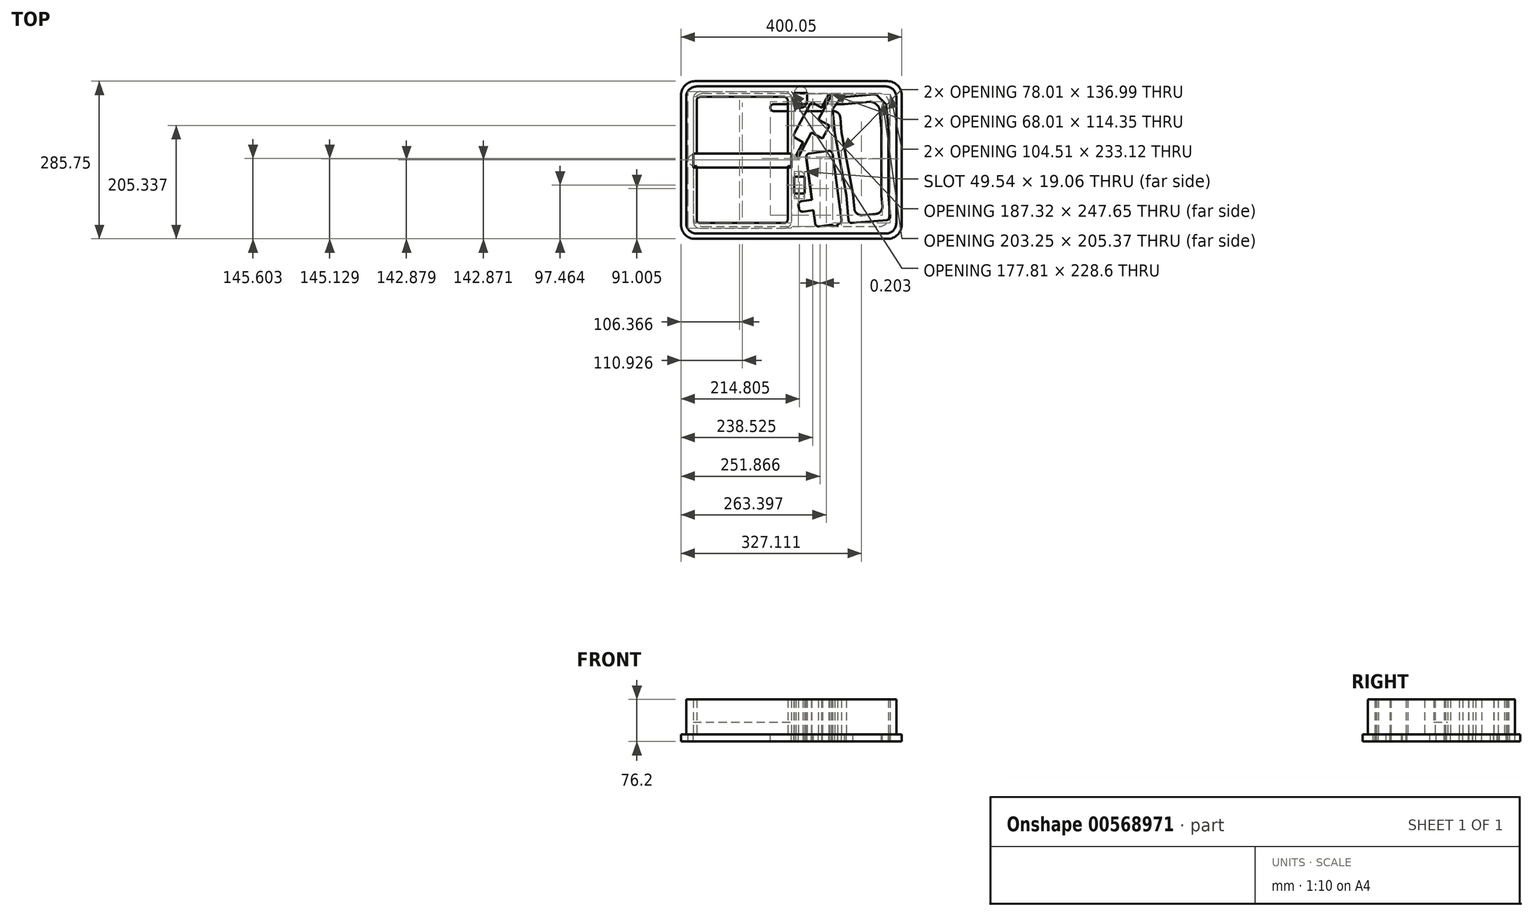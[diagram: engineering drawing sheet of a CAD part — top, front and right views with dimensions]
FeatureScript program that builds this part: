
annotation { "Feature Type Name" : "Feature", "Feature Type Description" : "" }
export const myFeature = defineFeature(function(context is Context, id is Id, definition is map)
    precondition{}
    {
        {
            var Q0;
            Q0=qCreatedBy(makeId("Top.planeOp"),FACE);
            var sketch = newSketch(context, id + "F0", { "sketchPlane" : qUnion([Q0])});
            skLineSegment(sketch, "E0.bottom", {"start": v(-171.53, 124.16) * mm, "end": v(171.37, 124.16) * mm});
            skLineSegment(sketch, "E0.top", {"start": v(-171.53, -142.54) * mm, "end": v(171.37, -142.54) * mm});
            skLineSegment(sketch, "E0.left", {"start": v(-190.58, 105.11) * mm, "end": v(-190.58, -123.49) * mm});
            skLineSegment(sketch, "E0.right", {"start": v(190.42, 105.11) * mm, "end": v(190.42, -123.49) * mm});
            skLineSegment(sketch, "E1.bottom", {"start": v(-165.18, 105.11) * mm, "end": v(-12.78, 105.11) * mm});
            skLineSegment(sketch, "E1.top", {"start": v(-165.18, -123.49) * mm, "end": v(-12.78, -123.49) * mm});
            skLineSegment(sketch, "E1.left", {"start": v(-171.53, 98.76) * mm, "end": v(-171.53, 2.24) * mm});
            skLineSegment(sketch, "E1.right", {"start": v(-6.43, 98.76) * mm, "end": v(-6.43, 2.24) * mm});
            skLineSegment(sketch, "E2.bottom", {"start": v(5.16, -39.36) * mm, "end": v(24.21, -39.36) * mm});
            skLineSegment(sketch, "E2.top", {"start": v(5.16, -69.84) * mm, "end": v(24.21, -69.84) * mm});
            skLineSegment(sketch, "E2.left", {"start": v(5.16, -39.36) * mm, "end": v(5.16, -69.84) * mm});
            skLineSegment(sketch, "E2.right", {"start": v(24.21, -39.36) * mm, "end": v(24.21, -69.84) * mm});
            skLineSegment(sketch, "E3", {"start": v(-25.48, 88.56) * mm, "end": v(62.79, 41.28) * mm, "construction": true});
            skLineSegment(sketch, "E4", {"start": v(19.13, 64.67) * mm, "end": v(5.33, 38.92) * mm});
            skLineSegment(sketch, "E5", {"start": v(7.93, 30.33) * mm, "end": v(21.37, 23.13) * mm});
            skLineSegment(sketch, "E6", {"start": v(21.37, 23.13) * mm, "end": v(8.17, -1.5) * mm});
            skLineSegment(sketch, "E7", {"start": v(8.17, -1.5) * mm, "end": v(12.65, -3.9) * mm});
            skLineSegment(sketch, "E8", {"start": v(48.93, 63.83) * mm, "end": v(69.08, 53.04) * mm});
            skLineSegment(sketch, "E9", {"start": v(69.08, 53.04) * mm, "end": v(62.79, 41.28) * mm});
            skPoint(sketch, "E10.visualSharp", {"position": v(2.33, 33.32) * mm});
            skArc(sketch, "E10.filletArc", {"start": v(5.33, 38.92) * mm, "mid": v(4.85, 34.09) * mm, "end": v(7.93, 30.33) * mm});
            skArc(sketch, "E11.MirrorCS", {"start": v(32.92, 90.42) * mm, "mid": v(36.68, 93.5) * mm, "end": v(41.51, 93.02) * mm});
            skLineSegment(sketch, "E12.MirrorCS", {"start": v(54.95, 85.82) * mm, "end": v(68.14, 110.45) * mm});
            skLineSegment(sketch, "E13.MirrorCS", {"start": v(41.51, 93.02) * mm, "end": v(54.95, 85.82) * mm});
            skPoint(sketch, "E14.MirrorP", {"position": v(35.92, 96.02) * mm});
            skLineSegment(sketch, "E15.MirrorCS", {"start": v(36.34, 40.32) * mm, "end": v(56.49, 29.53) * mm});
            skLineSegment(sketch, "E16.MirrorCS", {"start": v(19.13, 64.67) * mm, "end": v(32.92, 90.42) * mm});
            skLineSegment(sketch, "E17.MirrorCS", {"start": v(56.49, 29.53) * mm, "end": v(62.79, 41.28) * mm});
            skLineSegment(sketch, "E18", {"start": v(36.34, 40.32) * mm, "end": v(12.65, -3.9) * mm});
            skPoint(sketch, "E19.visualSharp", {"position": v(-190.58, 124.16) * mm});
            skArc(sketch, "E19.filletArc", {"start": v(-171.53, 124.16) * mm, "mid": v(-185, 118.58) * mm, "end": v(-190.58, 105.11) * mm});
            skPoint(sketch, "E20.visualSharp", {"position": v(190.42, 124.16) * mm});
            skArc(sketch, "E20.filletArc", {"start": v(190.42, 105.11) * mm, "mid": v(184.84, 118.58) * mm, "end": v(171.37, 124.16) * mm});
            skPoint(sketch, "E21.visualSharp", {"position": v(190.42, -142.54) * mm});
            skArc(sketch, "E21.filletArc", {"start": v(171.37, -142.54) * mm, "mid": v(184.84, -136.96) * mm, "end": v(190.42, -123.49) * mm});
            skPoint(sketch, "E22.visualSharp", {"position": v(-190.58, -142.54) * mm});
            skArc(sketch, "E22.filletArc", {"start": v(-190.58, -123.49) * mm, "mid": v(-185, -136.96) * mm, "end": v(-171.53, -142.54) * mm});
            skArc(sketch, "E23.filletArc", {"start": v(-165.18, 105.11) * mm, "mid": v(-169.67, 103.25) * mm, "end": v(-171.53, 98.76) * mm});
            skArc(sketch, "E24.filletArc", {"start": v(-171.53, -117.14) * mm, "mid": v(-169.67, -121.63) * mm, "end": v(-165.18, -123.49) * mm});
            skPoint(sketch, "E25.visualSharp", {"position": v(-6.43, 105.11) * mm});
            skArc(sketch, "E25.filletArc", {"start": v(-6.43, 98.76) * mm, "mid": v(-8.3, 103.25) * mm, "end": v(-12.78, 105.11) * mm});
            skPoint(sketch, "E26.visualSharp", {"position": v(-6.43, -123.49) * mm});
            skArc(sketch, "E26.filletArc", {"start": v(-12.78, -123.49) * mm, "mid": v(-8.3, -121.63) * mm, "end": v(-6.43, -117.14) * mm});
            skLineSegment(sketch, "E27.bottom", {"start": v(32.42, 2.65) * mm, "end": v(67.66, 7.4) * mm});
            skLineSegment(sketch, "E27.top", {"start": v(50.23, -129.5) * mm, "end": v(73.2, -126.41) * mm});
            skLineSegment(sketch, "E27.left", {"start": v(26.98, -4.5) * mm, "end": v(37.15, -80) * mm});
            skLineSegment(sketch, "E27.right", {"start": v(74.8, 1.95) * mm, "end": v(90.91, -117.62) * mm});
            skLineSegment(sketch, "E28.bottom", {"start": v(36.06, -81.44) * mm, "end": v(18.44, -83.81) * mm});
            skLineSegment(sketch, "E28.top", {"start": v(38.6, -100.32) * mm, "end": v(20.99, -102.7) * mm});
            skLineSegment(sketch, "E28.right", {"start": v(13, -90.95) * mm, "end": v(13.84, -97.25) * mm});
            skLineSegment(sketch, "E29.trimOffspring", {"start": v(40.03, -101.4) * mm, "end": v(43.09, -124.06) * mm});
            skLineSegment(sketch, "E30", {"start": v(37.32, -81.27) * mm, "end": v(39.86, -100.15) * mm, "construction": true});
            skPoint(sketch, "E31.visualSharp", {"position": v(26.13, 1.8) * mm});
            skArc(sketch, "E31.filletArc", {"start": v(32.42, 2.65) * mm, "mid": v(28.22, 0.2) * mm, "end": v(26.98, -4.5) * mm});
            skPoint(sketch, "E32.visualSharp", {"position": v(43.93, -130.35) * mm});
            skArc(sketch, "E32.filletArc", {"start": v(43.09, -124.06) * mm, "mid": v(45.53, -128.26) * mm, "end": v(50.23, -129.5) * mm});
            skPoint(sketch, "E33.visualSharp", {"position": v(91.76, -123.91) * mm});
            skArc(sketch, "E33.filletArc", {"start": v(85.47, -124.76) * mm, "mid": v(89.67, -122.32) * mm, "end": v(90.91, -117.62) * mm});
            skPoint(sketch, "E34.visualSharp", {"position": v(73.96, 8.24) * mm});
            skArc(sketch, "E34.filletArc", {"start": v(74.8, 1.95) * mm, "mid": v(72.36, 6.15) * mm, "end": v(67.66, 7.4) * mm});
            skPoint(sketch, "E35.visualSharp", {"position": v(12.15, -84.66) * mm});
            skArc(sketch, "E35.filletArc", {"start": v(18.44, -83.81) * mm, "mid": v(14.24, -86.25) * mm, "end": v(13, -90.95) * mm});
            skPoint(sketch, "E36.visualSharp", {"position": v(14.7, -103.54) * mm});
            skArc(sketch, "E36.filletArc", {"start": v(13.84, -97.25) * mm, "mid": v(16.29, -101.45) * mm, "end": v(20.99, -102.7) * mm});
            skLineSegment(sketch, "E37.bottom", {"start": v(5.33, 112.5) * mm, "end": v(28.44, 112.5) * mm});
            skLineSegment(sketch, "E37.left", {"start": v(5.33, 112.5) * mm, "end": v(5.33, 97.27) * mm});
            skLineSegment(sketch, "E37.right", {"start": v(28.44, 112.5) * mm, "end": v(28.44, 97.27) * mm});
            skArc(sketch, "E38", {"start": v(5.33, 97.27) * mm, "mid": v(16.89, 85.7) * mm, "end": v(28.44, 97.27) * mm});
            skLineSegment(sketch, "E39.bottom", {"start": v(73, 102.67) * mm, "end": v(170.4, 111.39) * mm, "construction": true});
            skLineSegment(sketch, "E39.top", {"start": v(93.38, -125.02) * mm, "end": v(190.78, -116.3) * mm, "construction": true});
            skLineSegment(sketch, "E39.left", {"start": v(73, 102.67) * mm, "end": v(93.38, -125.02) * mm, "construction": true});
            skLineSegment(sketch, "E39.right", {"start": v(170.4, 111.39) * mm, "end": v(190.78, -116.3) * mm, "construction": true});
            skLineSegment(sketch, "E40", {"start": v(121.7, 107.03) * mm, "end": v(142.08, -120.66) * mm, "construction": true});
            skLineSegment(sketch, "E41", {"start": v(90.08, 104.2) * mm, "end": v(110.45, -123.49) * mm, "construction": true});
            skLineSegment(sketch, "E42.MirrorCS", {"start": v(153.33, 109.86) * mm, "end": v(173.7, -117.83) * mm, "construction": true});
            skLineSegment(sketch, "E43", {"start": v(83.76, 103.64) * mm, "end": v(104.13, -124.06) * mm, "construction": true});
            skLineSegment(sketch, "E44.MirrorCS", {"start": v(159.65, 110.43) * mm, "end": v(180.02, -117.26) * mm, "construction": true});
            skLineSegment(sketch, "E45", {"start": v(74.76, 83.07) * mm, "end": v(172.16, 91.78) * mm, "construction": true});
            skLineSegment(sketch, "E46", {"start": v(78.66, 39.43) * mm, "end": v(176.06, 48.14) * mm, "construction": true});
            skLineSegment(sketch, "E47", {"start": v(89.41, -80.74) * mm, "end": v(186.82, -72.03) * mm, "construction": true});
            skLineSegment(sketch, "E48", {"start": v(92.96, 104.46) * mm, "end": v(150.45, 109.6) * mm});
            skLineSegment(sketch, "E49", {"start": v(155.41, 107.86) * mm, "end": v(170.44, 93.43) * mm});
            skLineSegment(sketch, "E50", {"start": v(172.37, 89.41) * mm, "end": v(176.06, 48.14) * mm});
            skLineSegment(sketch, "E51", {"start": v(176.06, 48.14) * mm, "end": v(176.06, -73) * mm});
            skLineSegment(sketch, "E52", {"start": v(176.06, -73) * mm, "end": v(179.46, -110.94) * mm});
            skLineSegment(sketch, "E53", {"start": v(173.7, -117.83) * mm, "end": v(110.45, -123.49) * mm});
            skLineSegment(sketch, "E54", {"start": v(103.56, -117.73) * mm, "end": v(99.56, -73) * mm});
            skLineSegment(sketch, "E55", {"start": v(99.56, -73) * mm, "end": v(78.66, 39.43) * mm});
            skLineSegment(sketch, "E56", {"start": v(78.66, 39.43) * mm, "end": v(74.97, 80.7) * mm});
            skLineSegment(sketch, "E57", {"start": v(76.15, 85) * mm, "end": v(88.38, 101.86) * mm});
            skPoint(sketch, "E58.visualSharp", {"position": v(104.13, -124.06) * mm});
            skArc(sketch, "E58.filletArc", {"start": v(103.56, -117.73) * mm, "mid": v(105.81, -122.04) * mm, "end": v(110.45, -123.49) * mm});
            skPoint(sketch, "E59.visualSharp", {"position": v(180.02, -117.26) * mm});
            skArc(sketch, "E59.filletArc", {"start": v(173.7, -117.83) * mm, "mid": v(178, -115.58) * mm, "end": v(179.46, -110.94) * mm});
            skPoint(sketch, "E60.visualSharp", {"position": v(90.08, 104.2) * mm});
            skArc(sketch, "E60.filletArc", {"start": v(92.96, 104.46) * mm, "mid": v(90.39, 103.66) * mm, "end": v(88.38, 101.86) * mm});
            skPoint(sketch, "E61.visualSharp", {"position": v(74.76, 83.07) * mm});
            skArc(sketch, "E61.filletArc", {"start": v(76.15, 85) * mm, "mid": v(75.17, 82.95) * mm, "end": v(74.97, 80.7) * mm});
            skPoint(sketch, "E62.visualSharp", {"position": v(153.33, 109.86) * mm});
            skArc(sketch, "E62.filletArc", {"start": v(155.41, 107.86) * mm, "mid": v(153.12, 109.27) * mm, "end": v(150.45, 109.6) * mm});
            skPoint(sketch, "E63.visualSharp", {"position": v(172.16, 91.78) * mm});
            skArc(sketch, "E63.filletArc", {"start": v(172.37, 89.41) * mm, "mid": v(171.77, 91.6) * mm, "end": v(170.44, 93.43) * mm});
            skLineSegment(sketch, "E64", {"start": v(5.33, 97.27) * mm, "end": v(28.44, 97.27) * mm, "construction": true});
            skLineSegment(sketch, "E65.MirrorCS", {"start": v(48.93, 63.83) * mm, "end": v(72.62, 108.05) * mm});
            skLineSegment(sketch, "E66.MirrorCS", {"start": v(68.14, 110.45) * mm, "end": v(72.62, 108.05) * mm});
            skLineSegment(sketch, "E67", {"start": v(84.07, -126.23) * mm, "end": v(84.15, -126.86) * mm});
            skLineSegment(sketch, "E68", {"start": v(83.06, -128.29) * mm, "end": v(76.14, -129.22) * mm});
            skLineSegment(sketch, "E69", {"start": v(74.71, -128.13) * mm, "end": v(74.63, -127.5) * mm});
            skLineSegment(sketch, "E70", {"start": v(85.15, -124.8) * mm, "end": v(85.47, -124.76) * mm});
            skPoint(sketch, "E71.visualSharp", {"position": v(39.86, -100.15) * mm});
            skArc(sketch, "E71.filletArc", {"start": v(40.03, -101.4) * mm, "mid": v(39.55, -100.57) * mm, "end": v(38.6, -100.32) * mm});
            skPoint(sketch, "E72.visualSharp", {"position": v(37.32, -81.27) * mm});
            skArc(sketch, "E72.filletArc", {"start": v(36.06, -81.44) * mm, "mid": v(36.9, -80.95) * mm, "end": v(37.15, -80) * mm});
            skPoint(sketch, "E73.visualSharp", {"position": v(74.88, -129.39) * mm});
            skArc(sketch, "E73.filletArc", {"start": v(74.71, -128.13) * mm, "mid": v(75.2, -128.97) * mm, "end": v(76.14, -129.22) * mm});
            skPoint(sketch, "E74.visualSharp", {"position": v(84.32, -128.12) * mm});
            skArc(sketch, "E74.filletArc", {"start": v(83.06, -128.29) * mm, "mid": v(83.9, -127.8) * mm, "end": v(84.15, -126.86) * mm});
            skPoint(sketch, "E75.visualSharp", {"position": v(83.9, -124.97) * mm});
            skArc(sketch, "E75.filletArc", {"start": v(85.15, -124.8) * mm, "mid": v(84.31, -125.29) * mm, "end": v(84.07, -126.23) * mm});
            skPoint(sketch, "E76.visualSharp", {"position": v(74.46, -126.24) * mm});
            skArc(sketch, "E76.filletArc", {"start": v(74.63, -127.5) * mm, "mid": v(74.14, -126.66) * mm, "end": v(73.2, -126.41) * mm});
            skLineSegment(sketch, "E77", {"start": v(73.2, -126.41) * mm, "end": v(85.15, -124.8) * mm, "construction": true});
            skLineSegment(sketch, "E78", {"start": v(-171.53, 2.24) * mm, "end": v(-177.9, 2.24) * mm});
            skLineSegment(sketch, "E79", {"start": v(-88.98, 105.11) * mm, "end": v(-88.98, -123.49) * mm, "construction": true});
            skLineSegment(sketch, "E80", {"start": v(-177.9, 2.24) * mm, "end": v(-177.9, -20.62) * mm});
            skLineSegment(sketch, "E81", {"start": v(-177.9, -20.62) * mm, "end": v(-171.53, -20.62) * mm});
            skLineSegment(sketch, "E82.MirrorCS", {"start": v(-6.43, 2.24) * mm, "end": v(-0.08, 2.24) * mm});
            skLineSegment(sketch, "E83.MirrorCS", {"start": v(-0.08, 2.24) * mm, "end": v(-0.08, -20.62) * mm});
            skLineSegment(sketch, "E84.MirrorCS", {"start": v(-0.08, -20.62) * mm, "end": v(-6.43, -20.62) * mm});
            skLineSegment(sketch, "E85", {"start": v(-171.53, -9.19) * mm, "end": v(-6.43, -9.19) * mm, "construction": true});
            skLineSegment(sketch, "E86", {"start": v(-177.9, -9.19) * mm, "end": v(-171.53, -9.19) * mm, "construction": true});
            skLineSegment(sketch, "E87", {"start": v(-171.53, 2.24) * mm, "end": v(-171.53, -20.62) * mm, "construction": true});
            skLineSegment(sketch, "E88", {"start": v(-171.53, -20.62) * mm, "end": v(-171.53, -117.14) * mm});
            skLineSegment(sketch, "E89", {"start": v(-6.43, 2.24) * mm, "end": v(-6.43, -20.62) * mm, "construction": true});
            skLineSegment(sketch, "E90", {"start": v(-6.43, -20.62) * mm, "end": v(-6.43, -117.14) * mm});
            skSolve(sketch);
        }
        {
            var Q0;
            Q0 = qSketchRegion(id + "F0", true);
            extrude(context, id + "F1", {"entities" : qUnion([Q0]), "depth" : 63.5 * mm, "offsetDistance" : 25.4 * mm});
        }
        {
            var Q0;
            Q0=qCreatedBy(makeId("Top.planeOp"),FACE);
            var sketch = newSketch(context, id + "F2", { "sketchPlane" : qUnion([Q0])});
            skLineSegment(sketch, "E91.0", {"start": v(-190.58, 124.16) * mm, "end": v(190.42, 124.16) * mm, "construction": true});
            skLineSegment(sketch, "E92.0", {"start": v(-190.58, 124.16) * mm, "end": v(-190.58, -142.54) * mm, "construction": true});
            skLineSegment(sketch, "E93.0", {"start": v(190.42, 124.16) * mm, "end": v(190.42, -142.54) * mm, "construction": true});
            skLineSegment(sketch, "E94.0", {"start": v(-190.26, -142.54) * mm, "end": v(190.42, -142.54) * mm, "construction": true});
            skPoint(sketch, "E95.orphan", {"position": v(-171.53, 124.16) * mm});
            skPoint(sketch, "E96.orphan", {"position": v(-190.58, 105.11) * mm});
            skPoint(sketch, "E97.orphan", {"position": v(171.37, 124.16) * mm});
            skPoint(sketch, "E98.orphan", {"position": v(190.42, 105.11) * mm});
            skPoint(sketch, "E99.orphan", {"position": v(190.42, -123.49) * mm});
            skPoint(sketch, "E100.orphan", {"position": v(171.37, -142.54) * mm});
            skPoint(sketch, "E101.orphan", {"position": v(-171.53, -142.54) * mm});
            skPoint(sketch, "E102.orphan", {"position": v(-190.58, -123.49) * mm});
            skPoint(sketch, "E103", {"position": v(0, 0) * mm});
            skLineSegment(sketch, "E104", {"start": v(-0.08, 124.16) * mm, "end": v(-0.08, -142.54) * mm, "construction": true});
            skPoint(sketch, "E104.startSnap0", {"position": v(-0.08, 124.16) * mm});
            skLineSegment(sketch, "E105", {"start": v(-190.58, -9.19) * mm, "end": v(190.42, -9.19) * mm, "construction": true});
            skPoint(sketch, "E106", {"position": v(-0.08, -9.19) * mm});
            skLineSegment(sketch, "E107.bottom", {"start": v(-158.83, 111.46) * mm, "end": v(158.67, 111.46) * mm});
            skLineSegment(sketch, "E107.top", {"start": v(-158.83, -129.84) * mm, "end": v(158.67, -129.84) * mm});
            skLineSegment(sketch, "E107.left", {"start": v(-177.88, 92.41) * mm, "end": v(-177.88, 9.86) * mm});
            skLineSegment(sketch, "E107.right", {"start": v(177.72, 92.41) * mm, "end": v(177.72, -110.79) * mm});
            skPoint(sketch, "E108.visualSharp", {"position": v(-177.88, 111.46) * mm});
            skPoint(sketch, "E109.visualSharp", {"position": v(177.72, 111.46) * mm});
            skPoint(sketch, "E110.visualSharp", {"position": v(177.72, -129.84) * mm});
            skPoint(sketch, "E111.visualSharp", {"position": v(-177.88, -129.84) * mm});
            skLineSegment(sketch, "E112.0.0", {"start": v(99.56, -73) * mm, "end": v(103.56, -117.73) * mm, "construction": true});
            skArc(sketch, "E112.0.1", {"start": v(103.56, -117.73) * mm, "mid": v(105.81, -122.04) * mm, "end": v(110.45, -123.49) * mm, "construction": true});
            skLineSegment(sketch, "E112.0.2", {"start": v(110.45, -123.49) * mm, "end": v(173.7, -117.83) * mm, "construction": true});
            skArc(sketch, "E112.0.3", {"start": v(173.7, -117.83) * mm, "mid": v(178, -115.58) * mm, "end": v(179.46, -110.94) * mm, "construction": true});
            skLineSegment(sketch, "E112.0.4", {"start": v(179.46, -110.94) * mm, "end": v(176.06, -73) * mm, "construction": true});
            skLineSegment(sketch, "E112.0.5", {"start": v(176.06, -73) * mm, "end": v(176.06, 48.14) * mm, "construction": true});
            skLineSegment(sketch, "E112.0.6", {"start": v(176.06, 48.14) * mm, "end": v(172.37, 89.41) * mm, "construction": true});
            skArc(sketch, "E112.0.7", {"start": v(172.37, 89.41) * mm, "mid": v(171.77, 91.6) * mm, "end": v(170.44, 93.43) * mm, "construction": true});
            skLineSegment(sketch, "E112.0.8", {"start": v(170.44, 93.43) * mm, "end": v(155.41, 107.86) * mm, "construction": true});
            skArc(sketch, "E112.0.9", {"start": v(155.41, 107.86) * mm, "mid": v(153.12, 109.27) * mm, "end": v(150.45, 109.6) * mm, "construction": true});
            skLineSegment(sketch, "E112.0.10", {"start": v(150.45, 109.6) * mm, "end": v(92.96, 104.46) * mm, "construction": true});
            skArc(sketch, "E112.0.11", {"start": v(92.96, 104.46) * mm, "mid": v(90.39, 103.66) * mm, "end": v(88.38, 101.86) * mm, "construction": true});
            skLineSegment(sketch, "E112.0.12", {"start": v(88.38, 101.86) * mm, "end": v(76.15, 85) * mm, "construction": true});
            skArc(sketch, "E112.0.13", {"start": v(76.15, 85) * mm, "mid": v(75.17, 82.95) * mm, "end": v(74.97, 80.7) * mm, "construction": true});
            skLineSegment(sketch, "E112.0.14", {"start": v(74.97, 80.7) * mm, "end": v(78.66, 39.43) * mm, "construction": true});
            skLineSegment(sketch, "E112.0.15", {"start": v(78.66, 39.43) * mm, "end": v(99.56, -73) * mm, "construction": true});
            skLineSegment(sketch, "E113.0", {"start": v(88.87, 67.9) * mm, "end": v(91.26, 41.16) * mm});
            skLineSegment(sketch, "E113.1", {"start": v(96.97, 92.07) * mm, "end": v(87.83, 79.46) * mm, "construction": true});
            skLineSegment(sketch, "E113.2", {"start": v(91.26, 41.16) * mm, "end": v(112.15, -71.26) * mm});
            skLineSegment(sketch, "E113.3", {"start": v(142.94, 96.18) * mm, "end": v(96.97, 92.07) * mm});
            skLineSegment(sketch, "E113.4", {"start": v(156.5, 89.2) * mm, "end": v(152.87, 92.7) * mm});
            skLineSegment(sketch, "E113.5", {"start": v(163.36, 47.57) * mm, "end": v(160.36, 81.18) * mm});
            skLineSegment(sketch, "E113.6", {"start": v(112.15, -71.26) * mm, "end": v(114.51, -97.62) * mm});
            skLineSegment(sketch, "E113.7", {"start": v(128.3, -109.14) * mm, "end": v(153.6, -106.88) * mm});
            skLineSegment(sketch, "E113.8", {"start": v(165.11, -93.1) * mm, "end": v(163.36, -73.56) * mm});
            skLineSegment(sketch, "E113.9", {"start": v(163.36, -73.56) * mm, "end": v(163.36, 47.57) * mm});
            skLineSegment(sketch, "E114", {"start": v(96.97, 92.07) * mm, "end": v(-31.83, 92.07) * mm});
            skLineSegment(sketch, "E115", {"start": v(-31.83, 92.07) * mm, "end": v(-31.83, 79.46) * mm, "construction": true});
            skLineSegment(sketch, "E116", {"start": v(-31.83, 79.46) * mm, "end": v(76.22, 79.46) * mm});
            skArc(sketch, "E117", {"start": v(-31.83, 92.07) * mm, "mid": v(-38.14, 85.76) * mm, "end": v(-31.83, 79.46) * mm});
            skPoint(sketch, "E118.visualSharp", {"position": v(115.65, -110.27) * mm});
            skArc(sketch, "E118.filletArc", {"start": v(114.51, -97.62) * mm, "mid": v(119.02, -106.24) * mm, "end": v(128.3, -109.14) * mm});
            skPoint(sketch, "E119.visualSharp", {"position": v(166.24, -105.75) * mm});
            skArc(sketch, "E119.filletArc", {"start": v(153.6, -106.88) * mm, "mid": v(162.2, -102.37) * mm, "end": v(165.11, -93.1) * mm});
            skPoint(sketch, "E120.visualSharp", {"position": v(87.83, 79.46) * mm});
            skArc(sketch, "E120.filletArc", {"start": v(88.87, 67.9) * mm, "mid": v(84.79, 76.13) * mm, "end": v(76.22, 79.46) * mm});
            skPoint(sketch, "E121.visualSharp", {"position": v(148.7, 96.7) * mm});
            skArc(sketch, "E121.filletArc", {"start": v(152.87, 92.7) * mm, "mid": v(148.29, 95.51) * mm, "end": v(142.94, 96.18) * mm});
            skPoint(sketch, "E122.visualSharp", {"position": v(159.93, 85.91) * mm});
            skArc(sketch, "E122.filletArc", {"start": v(160.36, 81.18) * mm, "mid": v(159.16, 85.54) * mm, "end": v(156.5, 89.2) * mm});
            skArc(sketch, "E123.filletArc", {"start": v(-158.83, 111.46) * mm, "mid": v(-172.3, 105.88) * mm, "end": v(-177.88, 92.41) * mm});
            skArc(sketch, "E124.filletArc", {"start": v(177.72, 92.41) * mm, "mid": v(172.14, 105.88) * mm, "end": v(158.67, 111.46) * mm});
            skArc(sketch, "E125.filletArc", {"start": v(158.67, -129.84) * mm, "mid": v(172.14, -124.26) * mm, "end": v(177.72, -110.79) * mm});
            skArc(sketch, "E126.filletArc", {"start": v(-177.88, -110.79) * mm, "mid": v(-172.3, -124.26) * mm, "end": v(-158.83, -129.84) * mm});
            skLineSegment(sketch, "E127", {"start": v(-177.88, 6.69) * mm, "end": v(-177.88, -25.06) * mm, "construction": true});
            skLineSegment(sketch, "E128", {"start": v(-177.88, -28.24) * mm, "end": v(-177.88, -110.79) * mm});
            skLineSegment(sketch, "E129", {"start": v(-177.88, -28.24) * mm, "end": v(-177.88, 9.86) * mm});
            skSolve(sketch);
        }
        {
            var Q0;
            Q0 = qSketchRegion(id + "F2", true);
            extrude(context, id + "F3", {"entities" : qUnion([Q0]), "oppositeDirection" : true, "depth" : 12.7 * mm, "offsetDistance" : 25.4 * mm});
        }
        {
            var Q0;
            Q0=qCreatedBy(makeId("Top.planeOp"),FACE);
            var sketch = newSketch(context, id + "F4", { "sketchPlane" : qUnion([Q0])});
            skLineSegment(sketch, "E130.bottom", {"start": v(-174.5, 133.7) * mm, "end": v(174.74, 133.7) * mm});
            skLineSegment(sketch, "E130.top", {"start": v(-174.5, -152.06) * mm, "end": v(174.74, -152.06) * mm});
            skLineSegment(sketch, "E130.left", {"start": v(-199.9, 108.3) * mm, "end": v(-199.9, -126.66) * mm});
            skLineSegment(sketch, "E130.right", {"start": v(200.14, 108.3) * mm, "end": v(200.14, -126.66) * mm});
            skLineSegment(sketch, "E131.bottom", {"start": v(-164.98, 114.64) * mm, "end": v(-12.58, 114.64) * mm});
            skLineSegment(sketch, "E131.top", {"start": v(-164.98, -133) * mm, "end": v(-12.58, -133) * mm});
            skLineSegment(sketch, "E131.left", {"start": v(-177.68, 101.94) * mm, "end": v(-177.68, 0.34) * mm});
            skLineSegment(sketch, "E131.right", {"start": v(0.12, 101.94) * mm, "end": v(0.12, -120.3) * mm});
            skLineSegment(sketch, "E132.left", {"start": v(5.36, -39.36) * mm, "end": v(5.36, -69.84) * mm});
            skLineSegment(sketch, "E133", {"start": v(-177, 169.84) * mm, "end": v(62.99, 41.3) * mm, "construction": true});
            skLineSegment(sketch, "E134", {"start": v(19.33, 64.68) * mm, "end": v(5.54, 38.93) * mm});
            skLineSegment(sketch, "E135", {"start": v(8.14, 30.33) * mm, "end": v(21.57, 23.14) * mm});
            skLineSegment(sketch, "E136", {"start": v(21.57, 23.14) * mm, "end": v(8.38, -1.5) * mm});
            skLineSegment(sketch, "E137", {"start": v(8.38, -1.5) * mm, "end": v(12.85, -3.89) * mm});
            skLineSegment(sketch, "E138", {"start": v(49.13, 63.84) * mm, "end": v(69.29, 53.05) * mm});
            skLineSegment(sketch, "E139", {"start": v(69.29, 53.05) * mm, "end": v(62.99, 41.3) * mm});
            skPoint(sketch, "E140.visualSharp", {"position": v(2.54, 33.33) * mm});
            skArc(sketch, "E140.filletArc", {"start": v(5.54, 38.93) * mm, "mid": v(5.06, 34.1) * mm, "end": v(8.14, 30.33) * mm});
            skArc(sketch, "E141.MirrorCS", {"start": v(33.12, 90.43) * mm, "mid": v(36.88, 93.5) * mm, "end": v(41.72, 93.03) * mm});
            skLineSegment(sketch, "E142.MirrorCS", {"start": v(55.15, 85.83) * mm, "end": v(68.34, 110.46) * mm});
            skLineSegment(sketch, "E143.MirrorCS", {"start": v(41.72, 93.03) * mm, "end": v(55.15, 85.83) * mm});
            skPoint(sketch, "E144.MirrorP", {"position": v(36.12, 96.03) * mm});
            skLineSegment(sketch, "E145.MirrorCS", {"start": v(36.54, 40.33) * mm, "end": v(56.7, 29.54) * mm});
            skLineSegment(sketch, "E146.MirrorCS", {"start": v(19.33, 64.68) * mm, "end": v(33.12, 90.43) * mm});
            skLineSegment(sketch, "E147.MirrorCS", {"start": v(56.7, 29.54) * mm, "end": v(62.99, 41.3) * mm});
            skLineSegment(sketch, "E148", {"start": v(36.54, 40.33) * mm, "end": v(12.85, -3.89) * mm});
            skPoint(sketch, "E149.visualSharp", {"position": v(-199.9, 133.7) * mm});
            skArc(sketch, "E149.filletArc", {"start": v(-174.5, 133.7) * mm, "mid": v(-192.47, 126.25) * mm, "end": v(-199.9, 108.3) * mm});
            skPoint(sketch, "E150.visualSharp", {"position": v(200.14, 133.7) * mm});
            skArc(sketch, "E150.filletArc", {"start": v(200.14, 108.3) * mm, "mid": v(192.7, 126.25) * mm, "end": v(174.74, 133.7) * mm});
            skPoint(sketch, "E151.visualSharp", {"position": v(200.14, -152.06) * mm});
            skArc(sketch, "E151.filletArc", {"start": v(174.74, -152.06) * mm, "mid": v(192.7, -144.62) * mm, "end": v(200.14, -126.66) * mm});
            skPoint(sketch, "E152.visualSharp", {"position": v(-199.9, -152.06) * mm});
            skArc(sketch, "E152.filletArc", {"start": v(-199.9, -126.66) * mm, "mid": v(-192.47, -144.62) * mm, "end": v(-174.5, -152.06) * mm});
            skPoint(sketch, "E153.visualSharp", {"position": v(-177.68, 114.64) * mm});
            skArc(sketch, "E153.filletArc", {"start": v(-164.98, 114.64) * mm, "mid": v(-173.96, 110.92) * mm, "end": v(-177.68, 101.94) * mm});
            skPoint(sketch, "E154.visualSharp", {"position": v(-177.68, -133) * mm});
            skArc(sketch, "E154.filletArc", {"start": v(-177.68, -120.3) * mm, "mid": v(-173.96, -129.29) * mm, "end": v(-164.98, -133) * mm});
            skPoint(sketch, "E155.visualSharp", {"position": v(0.12, 114.64) * mm});
            skArc(sketch, "E155.filletArc", {"start": v(0.12, 101.94) * mm, "mid": v(-3.6, 110.92) * mm, "end": v(-12.58, 114.64) * mm});
            skPoint(sketch, "E156.visualSharp", {"position": v(0.12, -133) * mm});
            skArc(sketch, "E156.filletArc", {"start": v(-12.58, -133) * mm, "mid": v(-3.6, -129.29) * mm, "end": v(0.12, -120.3) * mm});
            skLineSegment(sketch, "E157.bottom", {"start": v(32.63, 2.66) * mm, "end": v(67.87, 7.4) * mm});
            skLineSegment(sketch, "E157.top", {"start": v(50.43, -129.5) * mm, "end": v(73.39, -126.4) * mm});
            skLineSegment(sketch, "E157.left", {"start": v(27.18, -4.48) * mm, "end": v(37.52, -81.26) * mm});
            skLineSegment(sketch, "E157.right", {"start": v(75, 1.96) * mm, "end": v(91.12, -117.6) * mm});
            skLineSegment(sketch, "E158.top", {"start": v(40.07, -100.14) * mm, "end": v(21.19, -102.68) * mm});
            skLineSegment(sketch, "E158.right", {"start": v(13.2, -90.94) * mm, "end": v(14.05, -97.24) * mm});
            skLineSegment(sketch, "E159.trimOffspring", {"start": v(40.07, -100.14) * mm, "end": v(43.29, -124.05) * mm});
            skLineSegment(sketch, "E160", {"start": v(37.52, -81.26) * mm, "end": v(40.07, -100.14) * mm, "construction": true});
            skPoint(sketch, "E161.visualSharp", {"position": v(26.33, 1.8) * mm});
            skArc(sketch, "E161.filletArc", {"start": v(32.63, 2.66) * mm, "mid": v(28.42, 0.21) * mm, "end": v(27.18, -4.48) * mm});
            skPoint(sketch, "E162.visualSharp", {"position": v(44.14, -130.35) * mm});
            skArc(sketch, "E162.filletArc", {"start": v(43.29, -124.05) * mm, "mid": v(45.73, -128.25) * mm, "end": v(50.43, -129.5) * mm});
            skPoint(sketch, "E163.visualSharp", {"position": v(91.97, -123.9) * mm});
            skArc(sketch, "E163.filletArc", {"start": v(85.67, -124.75) * mm, "mid": v(89.87, -122.3) * mm, "end": v(91.12, -117.6) * mm});
            skPoint(sketch, "E164.visualSharp", {"position": v(74.16, 8.25) * mm});
            skArc(sketch, "E164.filletArc", {"start": v(75, 1.96) * mm, "mid": v(72.57, 6.16) * mm, "end": v(67.87, 7.4) * mm});
            skPoint(sketch, "E165.visualSharp", {"position": v(12.35, -84.65) * mm});
            skPoint(sketch, "E166.visualSharp", {"position": v(14.9, -103.53) * mm});
            skArc(sketch, "E166.filletArc", {"start": v(14.05, -97.24) * mm, "mid": v(16.5, -101.44) * mm, "end": v(21.19, -102.68) * mm});
            skLineSegment(sketch, "E167.bottom", {"start": v(5.53, 112.51) * mm, "end": v(28.65, 112.51) * mm, "construction": true});
            skLineSegment(sketch, "E167.left", {"start": v(5.53, 112.51) * mm, "end": v(5.53, 97.27) * mm});
            skLineSegment(sketch, "E167.right", {"start": v(28.65, 112.51) * mm, "end": v(28.65, 97.27) * mm});
            skArc(sketch, "E168", {"start": v(5.53, 97.27) * mm, "mid": v(17.1, 85.72) * mm, "end": v(28.65, 97.27) * mm});
            skLineSegment(sketch, "E169.bottom", {"start": v(73.2, 102.68) * mm, "end": v(170.6, 111.4) * mm, "construction": true});
            skLineSegment(sketch, "E169.top", {"start": v(93.58, -125) * mm, "end": v(190.98, -116.3) * mm, "construction": true});
            skLineSegment(sketch, "E169.left", {"start": v(73.2, 102.68) * mm, "end": v(93.58, -125) * mm, "construction": true});
            skLineSegment(sketch, "E169.right", {"start": v(170.6, 111.4) * mm, "end": v(190.98, -116.3) * mm, "construction": true});
            skLineSegment(sketch, "E170", {"start": v(121.9, 107.04) * mm, "end": v(142.28, -120.65) * mm, "construction": true});
            skLineSegment(sketch, "E171", {"start": v(90.28, 104.2) * mm, "end": v(110.66, -123.48) * mm, "construction": true});
            skLineSegment(sketch, "E172.MirrorCS", {"start": v(153.53, 109.87) * mm, "end": v(173.9, -117.82) * mm, "construction": true});
            skLineSegment(sketch, "E173", {"start": v(83.96, 103.64) * mm, "end": v(104.33, -124.05) * mm, "construction": true});
            skLineSegment(sketch, "E174.MirrorCS", {"start": v(159.85, 110.43) * mm, "end": v(180.23, -117.26) * mm, "construction": true});
            skLineSegment(sketch, "E175", {"start": v(74.96, 83.07) * mm, "end": v(172.36, 91.79) * mm, "construction": true});
            skLineSegment(sketch, "E176", {"start": v(78.87, 39.43) * mm, "end": v(176.27, 48.15) * mm, "construction": true});
            skLineSegment(sketch, "E177", {"start": v(89.62, -80.74) * mm, "end": v(187.02, -72.02) * mm, "construction": true});
            skLineSegment(sketch, "E178", {"start": v(93.16, 104.47) * mm, "end": v(150.65, 109.61) * mm});
            skLineSegment(sketch, "E179", {"start": v(155.62, 107.87) * mm, "end": v(170.65, 93.44) * mm});
            skLineSegment(sketch, "E180", {"start": v(172.57, 89.42) * mm, "end": v(176.27, 48.15) * mm});
            skLineSegment(sketch, "E181", {"start": v(176.27, 48.15) * mm, "end": v(176.27, -72.98) * mm});
            skLineSegment(sketch, "E182", {"start": v(176.27, -72.98) * mm, "end": v(179.66, -110.93) * mm});
            skLineSegment(sketch, "E183", {"start": v(173.9, -117.82) * mm, "end": v(110.66, -123.48) * mm});
            skLineSegment(sketch, "E184", {"start": v(103.76, -117.72) * mm, "end": v(99.76, -72.98) * mm});
            skLineSegment(sketch, "E185", {"start": v(99.76, -72.98) * mm, "end": v(78.87, 39.43) * mm});
            skLineSegment(sketch, "E186", {"start": v(78.87, 39.43) * mm, "end": v(75.17, 80.7) * mm});
            skLineSegment(sketch, "E187", {"start": v(76.36, 85) * mm, "end": v(88.59, 101.87) * mm});
            skPoint(sketch, "E188.visualSharp", {"position": v(104.33, -124.05) * mm});
            skArc(sketch, "E188.filletArc", {"start": v(103.76, -117.72) * mm, "mid": v(106.02, -122.03) * mm, "end": v(110.66, -123.48) * mm});
            skPoint(sketch, "E189.visualSharp", {"position": v(180.23, -117.26) * mm});
            skArc(sketch, "E189.filletArc", {"start": v(173.9, -117.82) * mm, "mid": v(178.2, -115.57) * mm, "end": v(179.66, -110.93) * mm});
            skPoint(sketch, "E190.visualSharp", {"position": v(90.28, 104.2) * mm});
            skArc(sketch, "E190.filletArc", {"start": v(93.16, 104.47) * mm, "mid": v(90.6, 103.66) * mm, "end": v(88.59, 101.87) * mm});
            skPoint(sketch, "E191.visualSharp", {"position": v(74.96, 83.07) * mm});
            skArc(sketch, "E191.filletArc", {"start": v(76.36, 85) * mm, "mid": v(75.38, 82.96) * mm, "end": v(75.17, 80.7) * mm});
            skPoint(sketch, "E192.visualSharp", {"position": v(153.53, 109.87) * mm});
            skArc(sketch, "E192.filletArc", {"start": v(155.62, 107.87) * mm, "mid": v(153.32, 109.28) * mm, "end": v(150.65, 109.61) * mm});
            skPoint(sketch, "E193.visualSharp", {"position": v(172.36, 91.79) * mm});
            skArc(sketch, "E193.filletArc", {"start": v(172.57, 89.42) * mm, "mid": v(171.97, 91.6) * mm, "end": v(170.65, 93.44) * mm});
            skLineSegment(sketch, "E194", {"start": v(5.53, 97.27) * mm, "end": v(28.65, 97.27) * mm, "construction": true});
            skLineSegment(sketch, "E195.MirrorCS", {"start": v(49.13, 63.84) * mm, "end": v(72.82, 108.06) * mm});
            skLineSegment(sketch, "E196.MirrorCS", {"start": v(68.34, 110.46) * mm, "end": v(72.82, 108.06) * mm});
            skLineSegment(sketch, "E197", {"start": v(0.12, 133.7) * mm, "end": v(0.12, -152.06) * mm, "construction": true});
            skPoint(sketch, "E198.endSnap0", {"position": v(180.8, -2.45) * mm});
            skLineSegment(sketch, "E199", {"start": v(-88.78, 114.64) * mm, "end": v(-88.78, -133) * mm, "construction": true});
            skLineSegment(sketch, "E200", {"start": v(-177.68, -9.18) * mm, "end": v(0.12, -9.18) * mm, "construction": true});
            skLineSegment(sketch, "E201", {"start": v(-199.9, -9.18) * mm, "end": v(200.14, -9.18) * mm, "construction": true});
            skArc(sketch, "E202", {"start": v(5.36, -69.84) * mm, "mid": v(14.9, -79.37) * mm, "end": v(24.43, -69.84) * mm});
            skArc(sketch, "E203", {"start": v(28.65, 112.51) * mm, "mid": v(17.1, 124.07) * mm, "end": v(5.53, 112.51) * mm});
            skArc(sketch, "E204", {"start": v(-177.68, 0.34) * mm, "mid": v(-187.2, -9.18) * mm, "end": v(-177.68, -18.7) * mm});
            skLineSegment(sketch, "E205", {"start": v(-177.68, 0.34) * mm, "end": v(-177.68, -18.7) * mm, "construction": true});
            skLineSegment(sketch, "E206", {"start": v(-177.68, -18.7) * mm, "end": v(-177.68, -120.3) * mm});
            skPoint(sketch, "E207.startSnap0", {"position": v(14.97, -29.83) * mm});
            skPoint(sketch, "E208.orphan", {"position": v(14.45, -79.36) * mm});
            skPoint(sketch, "E209.orphan", {"position": v(14.44, -84.65) * mm});
            skArc(sketch, "E210", {"start": v(24.43, -39.36) * mm, "mid": v(14.9, -29.83) * mm, "end": v(5.36, -39.36) * mm});
            skLineSegment(sketch, "E211", {"start": v(24.43, -69.84) * mm, "end": v(24.43, -39.36) * mm});
            skLineSegment(sketch, "E212", {"start": v(37.52, -81.26) * mm, "end": v(18.64, -83.8) * mm});
            skLineSegment(sketch, "E213", {"start": v(21.19, -102.68) * mm, "end": v(18.64, -83.8) * mm, "construction": true});
            skArc(sketch, "E214", {"start": v(18.64, -83.8) * mm, "mid": v(14.44, -86.24) * mm, "end": v(13.2, -90.94) * mm});
            skLineSegment(sketch, "E215", {"start": v(5.36, -39.36) * mm, "end": v(24.43, -39.36) * mm, "construction": true});
            skLineSegment(sketch, "E216", {"start": v(5.36, -69.84) * mm, "end": v(24.43, -69.84) * mm, "construction": true});
            skLineSegment(sketch, "E217", {"start": v(74.82, -127.5) * mm, "end": v(74.9, -128.12) * mm});
            skLineSegment(sketch, "E218", {"start": v(76.33, -129.21) * mm, "end": v(83.25, -128.28) * mm});
            skLineSegment(sketch, "E219", {"start": v(84.34, -126.85) * mm, "end": v(84.26, -126.22) * mm});
            skLineSegment(sketch, "E220", {"start": v(74.65, -126.24) * mm, "end": v(84.09, -124.96) * mm, "construction": true});
            skLineSegment(sketch, "E221", {"start": v(85.34, -124.8) * mm, "end": v(85.67, -124.75) * mm});
            skPoint(sketch, "E222.visualSharp", {"position": v(75.07, -129.38) * mm});
            skArc(sketch, "E222.filletArc", {"start": v(74.9, -128.12) * mm, "mid": v(75.39, -128.96) * mm, "end": v(76.33, -129.21) * mm});
            skPoint(sketch, "E223.visualSharp", {"position": v(84.51, -128.11) * mm});
            skArc(sketch, "E223.filletArc", {"start": v(83.25, -128.28) * mm, "mid": v(84.1, -127.8) * mm, "end": v(84.34, -126.85) * mm});
            skPoint(sketch, "E224.visualSharp", {"position": v(84.09, -124.96) * mm});
            skArc(sketch, "E224.filletArc", {"start": v(85.34, -124.8) * mm, "mid": v(84.5, -125.28) * mm, "end": v(84.26, -126.22) * mm});
            skPoint(sketch, "E225.visualSharp", {"position": v(74.65, -126.24) * mm});
            skArc(sketch, "E225.filletArc", {"start": v(74.82, -127.5) * mm, "mid": v(74.33, -126.65) * mm, "end": v(73.39, -126.4) * mm});
            skSolve(sketch);
        }
        {
            var Q0;
            Q0=makeQuery(id+"F4.imprint","IMPRINT",FACE,{"disambiguationData":[TD([[makeQuery(id+"F4.imprint","IMPRINT",EDGE,{"derivedFrom":sQuery(id+"F4.wireOp",EDGE,"E130.bottom")}),-1.0]])]});
            extrude(context, id + "F5", {"entities" : qUnion([Q0]), "oppositeDirection" : true, "depth" : 12.7 * mm, "offsetDistance" : 25.4 * mm});
        }
        {
            var Q0;
            Q0=makeQuery(id+"F1.opExtrude","SWEPT_FACE",FACE,{"disambiguationData":[OSD([sQuery(id+"F0.wireOp",EDGE,"E78")])]});
            var sketch = newSketch(context, id + "F6", { "sketchPlane" : qUnion([Q0])});
            skLineSegment(sketch, "E226.bottom", {"start": v(-177.9, 63.5) * mm, "end": v(-0.1, 63.5) * mm});
            skLineSegment(sketch, "E226.top", {"start": v(-177.9, 22.23) * mm, "end": v(-0.1, 22.23) * mm});
            skLineSegment(sketch, "E226.left", {"start": v(-177.9, 63.5) * mm, "end": v(-177.9, 22.23) * mm});
            skLineSegment(sketch, "E226.right", {"start": v(-0.1, 63.5) * mm, "end": v(-0.1, 22.23) * mm});
            skSolve(sketch);
        }
        {
            var Q0;
            Q0 = qSketchRegion(id + "F6", true);
            extrude(context, id + "F7", {"entities" : qUnion([Q0]), "depth" : 25.4 * mm, "offsetDistance" : 25.4 * mm});
        }
    });
